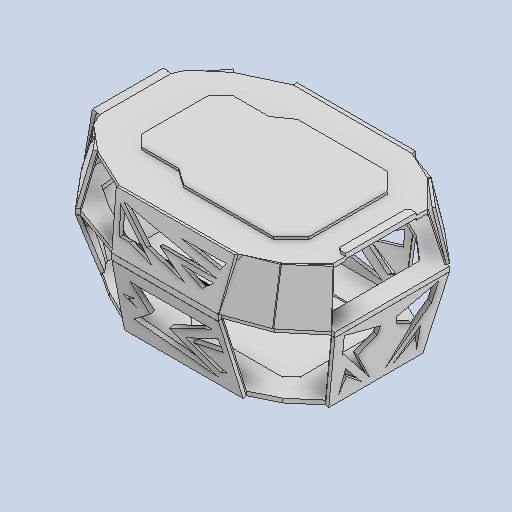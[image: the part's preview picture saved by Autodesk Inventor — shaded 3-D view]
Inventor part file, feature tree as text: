
AUTODESK INVENTOR PART (.ipt)
format: ipt  version: 2025.2 (Build 292293000, 293)  size: 842,752 bytes
history: native  units: mm
features: other x3, sketch x1
ambient origin geometry x8: Origin, YZ Plane, XZ Plane, XY Plane, X Axis, Y Axis, Z Axis, Center Point
bodies: Body1 (feature_tree)
feature tree (4):
  other  "Part1EDDv3.ipt"
  sketch  "Sketch1"  dims[d0=5.0mm d1=0.5mm]
  other  "Solid2::Part1EDDv3.ipt"
  other  "TaggingFeature1"
